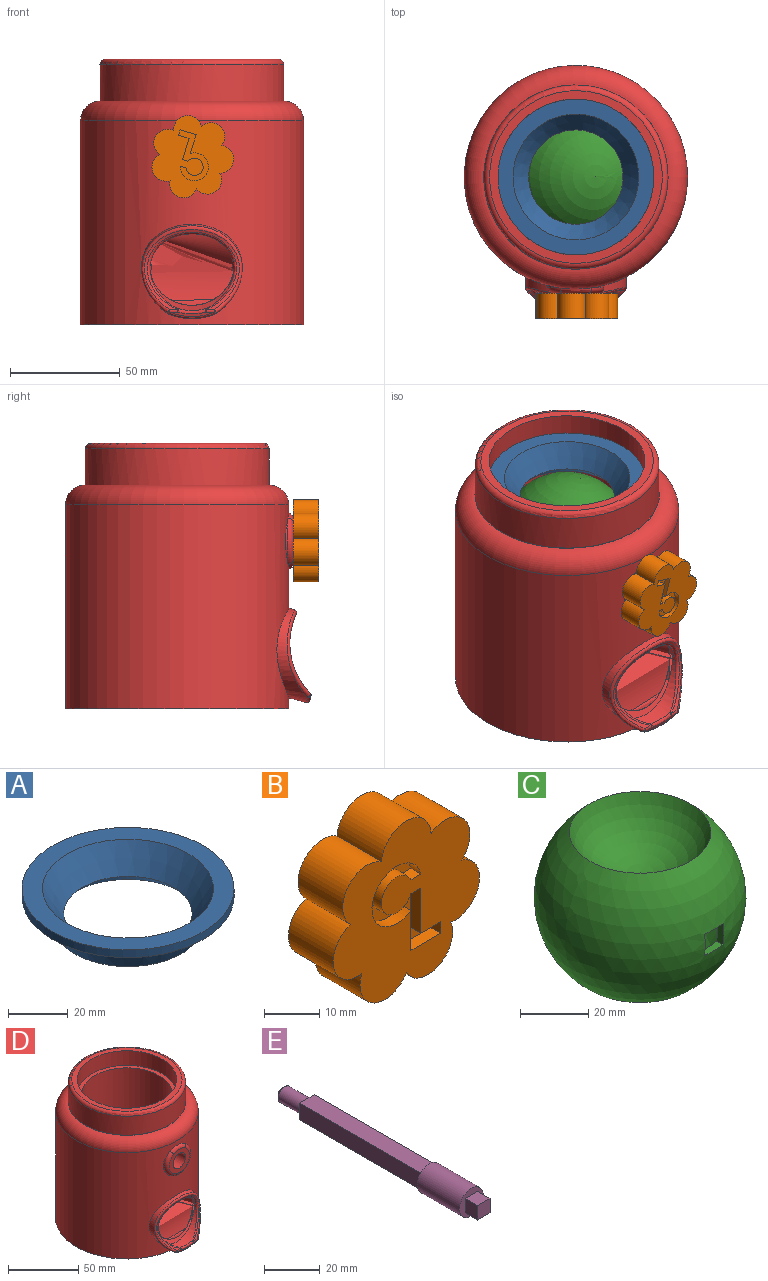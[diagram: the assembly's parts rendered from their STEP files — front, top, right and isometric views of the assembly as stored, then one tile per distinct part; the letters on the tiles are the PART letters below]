
ASSEMBLY  parts=5 mates=6
PART A: 6 faces, bbox 70.8x70.8x14 mm
  f0: sphere r=32.77mm, area 796.7mm2, adj f1,f5
  f1: cone r=29.07mm half-angle=19.5deg, axis (0,0,1), area 1964.4mm2, adj f0,f2
  f2: plane 70.85x70.85mm, normal (0,0,-1), area 1286.7mm2, adj f1,f3
  f3: cylinder r=35.42mm len=70.85mm, axis (0,0,-1), area 706.7mm2, adj f2,f4
  f4: plane 70.85x70.85mm, normal (0,0,1), area 1378.7mm2, adj f3,f5
  f5: cone r=21.45mm half-angle=35deg, axis (0,0,1), area 1948.9mm2, adj f0,f4
PART B: 24 faces, bbox 37.5x11.4x36.8 mm
  f0: plane 37.46x36.84mm, normal (0,1,0), area 944.4mm2, adj f2,f3,f4,f5,f6,f7,f8,f19
  f1: plane 37.46x36.84mm, normal (0,-1,0), area 877mm2, adj f2,f3,f4,f5,f6,f7,f8,f9
  f2: cylinder r=6.35mm len=11.43mm, axis (0,1,0), area 217.7mm2, adj f0,f1,f3,f8
  f3: cylinder r=6.35mm len=12.67mm, axis (0,1,0), area 217.7mm2, adj f0,f1,f2,f4
  f4: cylinder r=6.35mm len=11.43mm, axis (0,1,0), area 217.7mm2, adj f0,f1,f3,f5
  f5: cylinder r=6.35mm len=12.42mm, axis (0,1,0), area 217.7mm2, adj f0,f1,f4,f6
  f6: cylinder r=6.35mm len=11.86mm, axis (0,1,0), area 217.7mm2, adj f0,f1,f5,f7
  f7: cylinder r=6.35mm len=11.86mm, axis (0,1,0), area 217.7mm2, adj f0,f1,f6,f8
  f8: cylinder r=6.35mm len=12.42mm, axis (0,1,0), area 217.7mm2, adj f0,f1,f2,f7
  f9: cylinder r=3.94mm len=7.87mm, axis (0,-1,0), area 54.7mm2, adj f1,f10,f17,f18
  f10: plane 2.54x2.54mm, normal (0,0,1), area 6.5mm2, adj f1,f9,f11,f18
  f11: cylinder r=6.35mm len=12.7mm, axis (0,-1,0), area 81.8mm2, adj f1,f10,f12,f18
  f12: plane 8.89x2.54mm, normal (1,0,0), area 22.6mm2, adj f1,f11,f13,f18
  f13: plane 7.62x2.54mm, normal (0,0,1), area 19.4mm2, adj f1,f12,f14,f18
  f14: plane 2.54x2.54mm, normal (-1,0,0), area 6.5mm2, adj f1,f13,f15,f18
  f15: plane 5.08x2.54mm, normal (0,0,-1), area 12.9mm2, adj f1,f14,f16,f18
  f16: plane 10.02x2.54mm, normal (-1,0,0), area 25.4mm2, adj f1,f15,f17,f18
  f17: plane 2.54x2.54mm, normal (0,0,-1), area 6.5mm2, adj f1,f9,f16,f18
  f18: plane 20.46x17.59mm, normal (0,-1,0), area 109.3mm2, adj f9,f10,f11,f12,f13,f14,f15,f16
  f19: plane 6.48x6.35mm, normal (0,0,1), area 41.1mm2, adj f0,f20,f22,f23
  f20: plane 6.48x6.35mm, normal (1,0,0), area 41.1mm2, adj f0,f19,f21,f23
  f21: plane 6.48x6.35mm, normal (0,0,-1), area 41.1mm2, adj f0,f20,f22,f23
  f22: plane 6.48x6.35mm, normal (-1,0,0), area 41.1mm2, adj f0,f19,f21,f23
  f23: plane 6.48x6.48mm, normal (0,1,0), area 42mm2, adj f19,f20,f21,f22
PART C: 12 faces, bbox 62.2x62.2x54.3 mm
  f0: sphere r=24.77mm, area 1940.9mm2, adj f1
  f1: sphere r=28.57mm, area 8393.1mm2, adj f0,f2,f3,f4,f5,f6,f7,f8
  f2: plane 7.62x2.82mm, normal (0,0,1), area 19.6mm2, adj f1,f3,f5,f10
  f3: plane 7.62x2.82mm, normal (1,0,0), area 19.6mm2, adj f1,f2,f4,f10
  f4: plane 7.62x2.82mm, normal (0,0,-1), area 19.6mm2, adj f1,f3,f5,f10
  f5: plane 7.62x2.82mm, normal (-1,0,0), area 19.6mm2, adj f1,f2,f4,f10
  f6: plane 7.62x2.82mm, normal (-1,0,0), area 19.6mm2, adj f1,f7,f9,f10
  f7: plane 7.62x2.82mm, normal (0,0,-1), area 19.6mm2, adj f1,f6,f8,f10
  f8: plane 7.62x2.82mm, normal (1,0,0), area 19.6mm2, adj f1,f7,f9,f10
  f9: plane 7.62x2.82mm, normal (0,0,1), area 19.6mm2, adj f1,f6,f8,f10
  f10: sphere r=31.12mm, area 10497.5mm2, adj f2,f3,f4,f5,f6,f7,f8,f9
  f11: sphere r=22.23mm, area 1995.2mm2, adj f10
PART D: 50 faces, bbox 110x123.9x120.7 mm
  f0: cylinder r=50.8mm len=101.6mm, axis (0,0,1), area 27621mm2, adj f1,f15,f36,f37,f38,f39,f40
  f1: extruded ~45.52x43.11mm, area 682.2mm2, adj f0,f2,f14
  f2: bspline ~25.47x4.39mm, area 43.2mm2, adj f1,f3,f12,f13
  f3: plane 20.36x2.11mm, normal (0,-0.97,-0.26), area 22mm2, adj f2,f4,f10,f11
  f4: cylinder r=1.27mm len=3.65mm, axis (1,0,0), area 4.8mm2, adj f3,f5,f9,f13
  f5: cylinder r=32.47mm len=43.18mm, axis (1,0,0), area 149.9mm2, adj f4,f6,f11,f14
  f6: bspline ~40.67x35.59mm, area 182.3mm2, adj f5,f7,f8,f9
  f7: sphere r=1.27mm, area 0.6mm2, adj f6,f10,f11
  f8: extruded ~36.04x33.79mm, area 8249mm2, adj f6,f10,f49
  f9: sphere r=1.27mm, area 0.6mm2, adj f4,f6,f10
  f10: bspline ~15.65x2.78mm, area 25.5mm2, adj f3,f7,f8,f9
  f11: cylinder r=1.27mm len=3.65mm, axis (1,0,0), area 4.8mm2, adj f3,f5,f7,f12
  f12: sphere r=1.27mm, area 1.4mm2, adj f2,f11,f14
  f13: sphere r=1.27mm, area 1.6mm2, adj f2,f4,f14
  f14: bspline ~45.77x40.7mm, area 264.1mm2, adj f1,f5,f12,f13
  f15: bspline ~16.04x5.1mm, area 51.4mm2, adj f0,f16,f17,f18
  f16: torus R=10.16mm, axis (0,-1,0), area 91.3mm2, adj f15,f18,f36,f37
  f17: torus R=10.16mm, axis (0,-1,0), area 91.3mm2, adj f15,f18,f37,f38
  f18: plane 20.44x20.32mm, normal (0,-1,0), area 198.3mm2, adj f15,f16,f17,f19,f37
  f19: cylinder r=6.35mm len=20.57mm, axis (0,1,0), area 820.9mm2, adj f18,f20
  f20: cylinder r=32.26mm len=64.52mm, axis (0,0,1), area 10385.6mm2, adj f19,f21,f23,f29
  f21: cylinder r=3.56mm len=12.7mm, axis (0,-1,0), area 283.8mm2, adj f20,f22
  f22: plane 7.11x7.11mm, normal (0,-1,0), area 39.7mm2, adj f21
  f23: plane 70.87x70.87mm, normal (0,0,1), area 675.2mm2, adj f20,f24
  f24: cylinder r=35.43mm len=70.87mm, axis (0,0,1), area 2827.4mm2, adj f23,f25
  f25: plane 78.49x78.49mm, normal (0,0,1), area 893.8mm2, adj f24,f26
  f26: torus R=39.24mm, axis (0,0,-1), area 1024.3mm2, adj f25,f27
  f27: cylinder r=41.78mm len=83.57mm, axis (0,0,1), area 4334.4mm2, adj f26,f28
  f28: plane 83.82x83.82mm, normal (0,0,1), area 33.4mm2, adj f27,f39
  f29: torus R=20.83mm, axis (0,0,-1), area 2143.1mm2, adj f20,f30,f33,f34,f35
  f30: bspline ~11.25x9.99mm, area 62.5mm2, adj f29,f31,f33,f35
  f31: bspline ~38.13x17.2mm, area 342.1mm2, adj f30,f32,f34,f49
  f32: plane 26.01x6.65mm, normal (0,-0.97,-0.26), area 104.1mm2, adj f31,f33
  f33: bspline ~30.61x7.54mm, area 175.8mm2, adj f29,f30,f32,f34
  f34: bspline ~11.89x11.13mm, area 62.5mm2, adj f29,f31,f33,f35
  f35: bspline ~53.38x46.21mm, area 886.8mm2, adj f29,f30,f34,f49
  f36: cylinder r=12.7mm len=20.97mm, axis (0,1,0), area 0mm2, adj f0,f16
  f37: bspline ~16.04x5.1mm, area 51.4mm2, adj f0,f16,f17,f18
  f38: cylinder r=12.7mm len=20.97mm, axis (0,1,0), area 0mm2, adj f0,f17
  f39: torus R=41.91mm, axis (0,0,1), area 4173.8mm2, adj f0,f28
  f40: plane 101.6x101.6mm, normal (0,0,-1), area 8075.7mm2, adj f0,f41,f43,f45,f47
  f41: cylinder r=1.59mm len=25.4mm, axis (0,0,-1), area 253.4mm2, adj f40,f42
  f42: plane 3.18x3.18mm, normal (0,0,-1), area 7.9mm2, adj f41
  f43: cylinder r=1.59mm len=25.4mm, axis (0,0,-1), area 253.4mm2, adj f40,f44
  f44: plane 3.18x3.18mm, normal (0,0,-1), area 7.9mm2, adj f43
  f45: cylinder r=1.59mm len=25.4mm, axis (0,0,-1), area 253.4mm2, adj f40,f46
  f46: plane 3.18x3.18mm, normal (0,0,-1), area 7.9mm2, adj f45
  f47: cylinder r=1.59mm len=25.4mm, axis (0,0,-1), area 253.4mm2, adj f40,f48
  f48: plane 3.18x3.18mm, normal (0,0,-1), area 7.9mm2, adj f47
  f49: extruded ~79.04x49.61mm, area 18345mm2, adj f8,f31,f35
PART E: 16 faces, bbox 12.2x102.8x12.2 mm
  f0: plane 12.19x12.19mm, normal (0,-1,0), area 76.2mm2, adj f7,f11,f12,f13,f14
  f1: plane 7.37x7.37mm, normal (0,1,0), area 20mm2, adj f2,f3,f4,f5,f8
  f2: plane 62.23x7.37mm, normal (-1,0,0), area 458.4mm2, adj f1,f3,f5,f6
  f3: plane 62.23x7.37mm, normal (0,0,1), area 458.4mm2, adj f1,f2,f4,f6
  f4: plane 62.23x7.37mm, normal (1,0,0), area 458.4mm2, adj f1,f3,f5,f6
  f5: plane 62.23x7.37mm, normal (0,0,-1), area 458.4mm2, adj f1,f2,f4,f6
  f6: plane 12.19x12.19mm, normal (0,1,0), area 62.5mm2, adj f2,f3,f4,f5,f7
  f7: cylinder r=6.1mm len=21.59mm, axis (0,1,0), area 826.9mm2, adj f0,f6
  f8: cylinder r=3.3mm len=11.43mm, axis (0,-1,0), area 237.1mm2, adj f1,f10
  f9: plane 4.06x4.06mm, normal (0,1,0), area 13mm2, adj f10
  f10: cone r=2.03mm half-angle=45deg, axis (0,-1,0), area 30.1mm2, adj f8,f9
  f11: plane 6.35x6.3mm, normal (0,0,-1), area 40mm2, adj f0,f12,f14,f15
  f12: plane 6.39x6.3mm, normal (1,0,0), area 40.3mm2, adj f0,f11,f13,f15
  f13: plane 6.35x6.3mm, normal (0,0,1), area 40mm2, adj f0,f12,f14,f15
  f14: plane 6.39x6.3mm, normal (-1,0,0), area 40.3mm2, adj f0,f11,f13,f15
  f15: plane 6.39x6.35mm, normal (0,-1,0), area 40.6mm2, adj f11,f12,f13,f14
PLACE A t=(2.02,3.88,11.42)mm
PLACE B rot(axis=(0,-1,0),162.8deg) t=(2.02,-27.36,11.42)mm
PLACE C rot(axis=(0,-1,0),162.8deg) t=(1.93,4.23,11.58)mm
PLACE D t=(2.02,3.88,-4.46)mm fixed
PLACE E rot(axis=(0,1,0),17.2deg) t=(2.02,-27.36,11.42)mm
MATE fastened A.f1 <-> D.f39  axis (0,0,-1) through (2.02,3.88,43.17)mm
MATE planar C.f7 <-> E.f5  axis (0.3,0,0.96) through (0.81,-25.29,7.94)mm
MATE revolute E.f7 <-> D.f16  axis (0,-1,0) through (2.02,-48.95,11.42)mm
MATE planar C.f8 <-> E.f4  axis (-0.96,0,0.3) through (5.57,-25.29,10.45)mm
MATE planar C.f4 <-> E.f5  axis (-0.3,0,-0.96) through (4.45,34.87,6.81)mm
MATE fastened B.f0 <-> E.f7  axis (0,1,0) through (2.02,-48.95,11.42)mm
